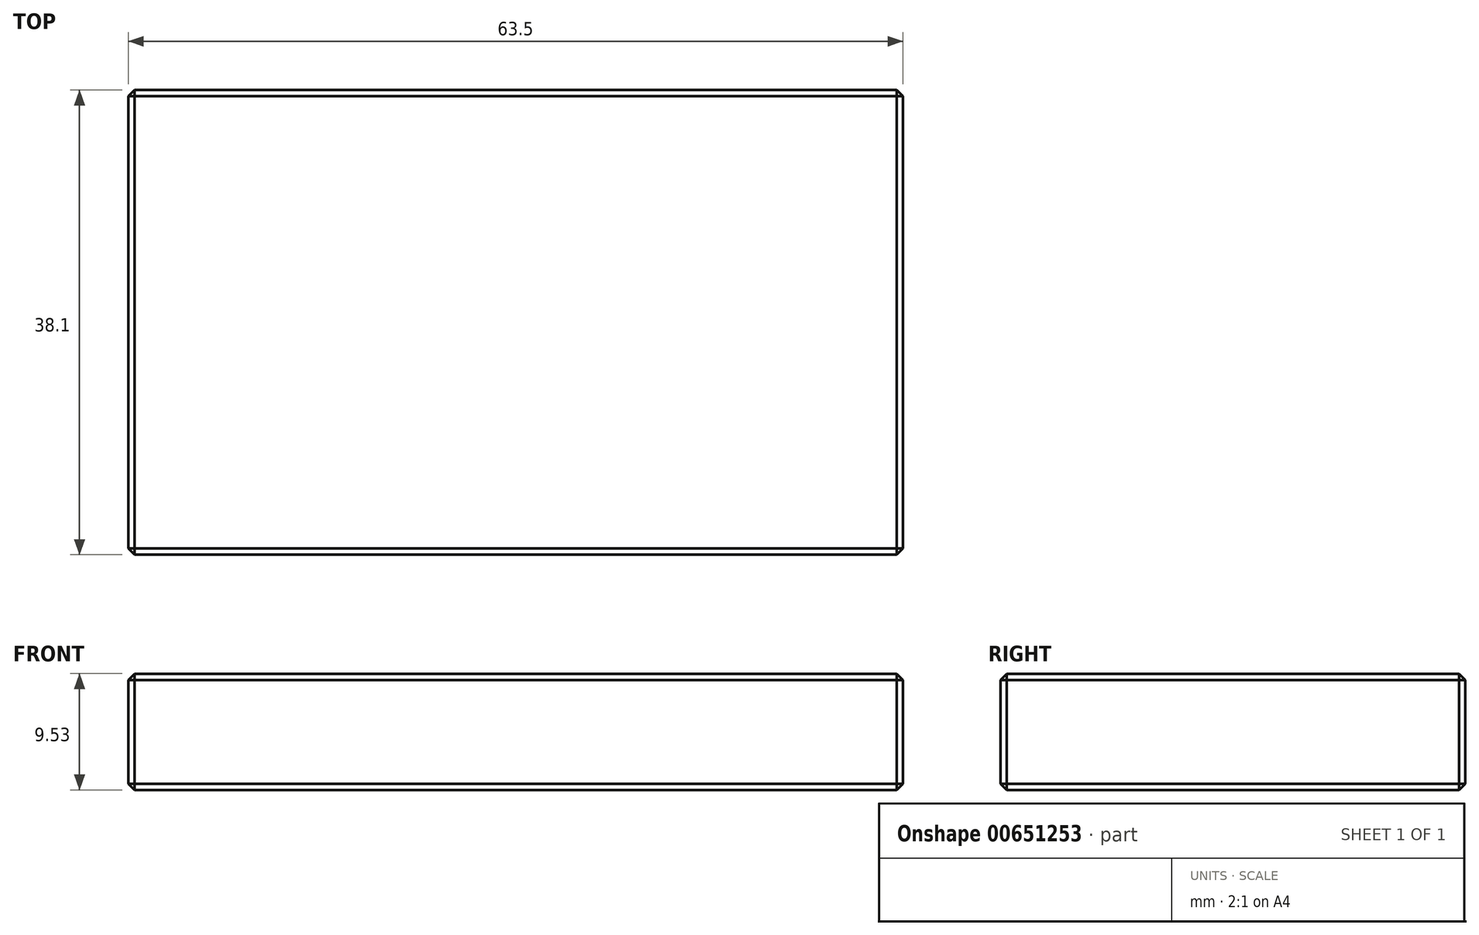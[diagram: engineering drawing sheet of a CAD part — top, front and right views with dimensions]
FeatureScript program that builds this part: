
annotation { "Feature Type Name" : "Feature", "Feature Type Description" : "" }
export const myFeature = defineFeature(function(context is Context, id is Id, definition is map)
    precondition{}
    {
        {
            var Q0;
            Q0=qCreatedBy(makeId("Top.planeOp"),FACE);
            var sketch = newSketch(context, id + "F0", { "sketchPlane" : qUnion([Q0])});
            skLineSegment(sketch, "E0.bottom", {"start": v(31.75, -19.05) * mm, "end": v(-31.75, -19.05) * mm});
            skLineSegment(sketch, "E0.top", {"start": v(31.75, 19.05) * mm, "end": v(-31.75, 19.05) * mm});
            skLineSegment(sketch, "E0.left", {"start": v(31.75, -19.05) * mm, "end": v(31.75, 19.05) * mm});
            skLineSegment(sketch, "E0.right", {"start": v(-31.75, -19.05) * mm, "end": v(-31.75, 19.05) * mm});
            skPoint(sketch, "E0.middle", {"position": v(0, 0) * mm});
            skSolve(sketch);
        }
        {
            var Q0;
            Q0=makeQuery(id+"F0.imprint","IMPRINT",FACE,{"disambiguationData":[TD([[makeQuery(id+"F0.imprint","IMPRINT",EDGE,{"derivedFrom":sQuery(id+"F0.wireOp",EDGE,"E0.bottom")}),-1.0]])]});
            extrude(context, id + "F1", {"entities" : qUnion([Q0]), "depth" : 9.52 * mm, "offsetDistance" : 25.4 * mm});
        }
        {
            var Q0;
            Q0=makeQuery(id+"F1.opExtrude","SWEPT_FACE",FACE,{"disambiguationData":[OSD([sQuery(id+"F0.wireOp",EDGE,"E0.bottom")])]});
            var Q1;
            Q1=makeQuery(id+"F1.opExtrude","SWEPT_FACE",FACE,{"disambiguationData":[OSD([sQuery(id+"F0.wireOp",EDGE,"E0.left")])]});
            var Q2;
            Q2=makeQuery(id+"F1.opExtrude","CAP_FACE",FACE,{"disambiguationData":[OSD([sQuery(id+"F0.wireOp",EDGE,"E0.bottom"),sQuery(id+"F0.wireOp",EDGE,"E0.top"),sQuery(id+"F0.wireOp",EDGE,"E0.left"),sQuery(id+"F0.wireOp",EDGE,"E0.right")])],"isStart":true});
            var Q3;
            Q3=makeQuery(id+"F1.opExtrude","SWEPT_FACE",FACE,{"disambiguationData":[OSD([sQuery(id+"F0.wireOp",EDGE,"E0.top")])]});
            var Q4;
            Q4=makeQuery(id+"F1.opExtrude","SWEPT_FACE",FACE,{"disambiguationData":[OSD([sQuery(id+"F0.wireOp",EDGE,"E0.right")])]});
            chamfer(context, id + "F2", {"entities" : qUnion([Q0, Q1, Q2, Q3, Q4]), "width" : 0.5 * mm, "tangentPropagation" : true});
        }
    });
